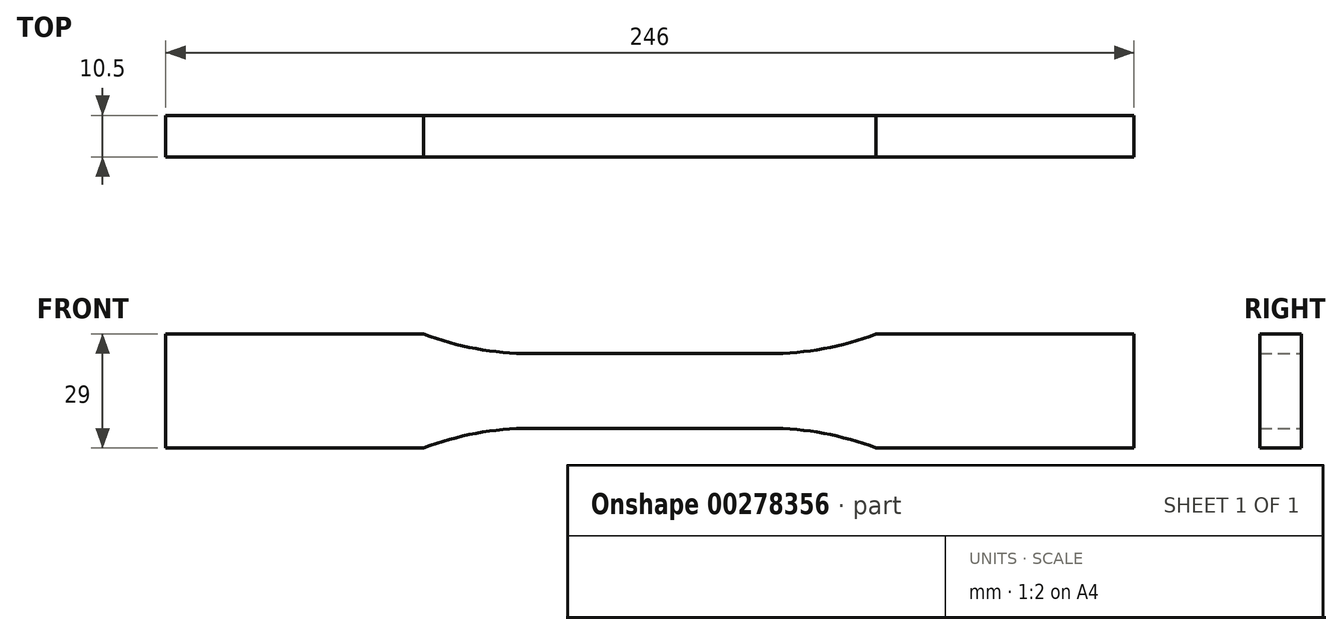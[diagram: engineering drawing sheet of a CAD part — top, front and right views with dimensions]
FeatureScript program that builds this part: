
annotation { "Feature Type Name" : "Feature", "Feature Type Description" : "" }
export const myFeature = defineFeature(function(context is Context, id is Id, definition is map)
    precondition{}
    {
        {
            var Q0;
            Q0=qCreatedBy(makeId("Front.planeOp"),FACE);
            var sketch = newSketch(context, id + "F0", { "sketchPlane" : qUnion([Q0])});
            skLineSegment(sketch, "E0", {"start": v(0, 9.5) * mm, "end": v(30.39, 9.5) * mm});
            skArc(sketch, "E1", {"start": v(30.39, 9.5) * mm, "mid": v(44.17, 10.76) * mm, "end": v(57.5, 14.5) * mm});
            skLineSegment(sketch, "E2", {"start": v(57.5, 14.5) * mm, "end": v(123, 14.5) * mm});
            skLineSegment(sketch, "E3.MirrorCS", {"start": v(57.5, -14.5) * mm, "end": v(123, -14.5) * mm});
            skLineSegment(sketch, "E4.MirrorCS", {"start": v(0, -9.5) * mm, "end": v(30.39, -9.5) * mm});
            skArc(sketch, "E5.MirrorCS", {"start": v(30.39, -9.5) * mm, "mid": v(44.17, -10.76) * mm, "end": v(57.5, -14.5) * mm});
            skArc(sketch, "E6.MirrorCS", {"start": v(-30.39, -9.5) * mm, "mid": v(-44.17, -10.76) * mm, "end": v(-57.5, -14.5) * mm});
            skLineSegment(sketch, "E7.MirrorCS", {"start": v(0, 9.5) * mm, "end": v(-30.39, 9.5) * mm});
            skArc(sketch, "E8.MirrorCS", {"start": v(-30.39, 9.5) * mm, "mid": v(-44.17, 10.76) * mm, "end": v(-57.5, 14.5) * mm});
            skLineSegment(sketch, "E9.MirrorCS", {"start": v(-57.5, -14.5) * mm, "end": v(-123, -14.5) * mm});
            skLineSegment(sketch, "E10.MirrorCS", {"start": v(0, -9.5) * mm, "end": v(-30.39, -9.5) * mm});
            skLineSegment(sketch, "E11.MirrorCS", {"start": v(-57.5, 14.5) * mm, "end": v(-123, 14.5) * mm});
            skLineSegment(sketch, "E12", {"start": v(-123, -14.5) * mm, "end": v(-123, 14.5) * mm});
            skLineSegment(sketch, "E13", {"start": v(123, -14.5) * mm, "end": v(123, 14.5) * mm});
            skSolve(sketch);
        }
        {
            var Q0;
            Q0 = qSketchRegion(id + "F0", true);
            extrude(context, id + "F1", {"entities" : qUnion([Q0]), "endBound" : BoundingType.SYMMETRIC, "depth" : 10.5 * mm});
        }
    });
